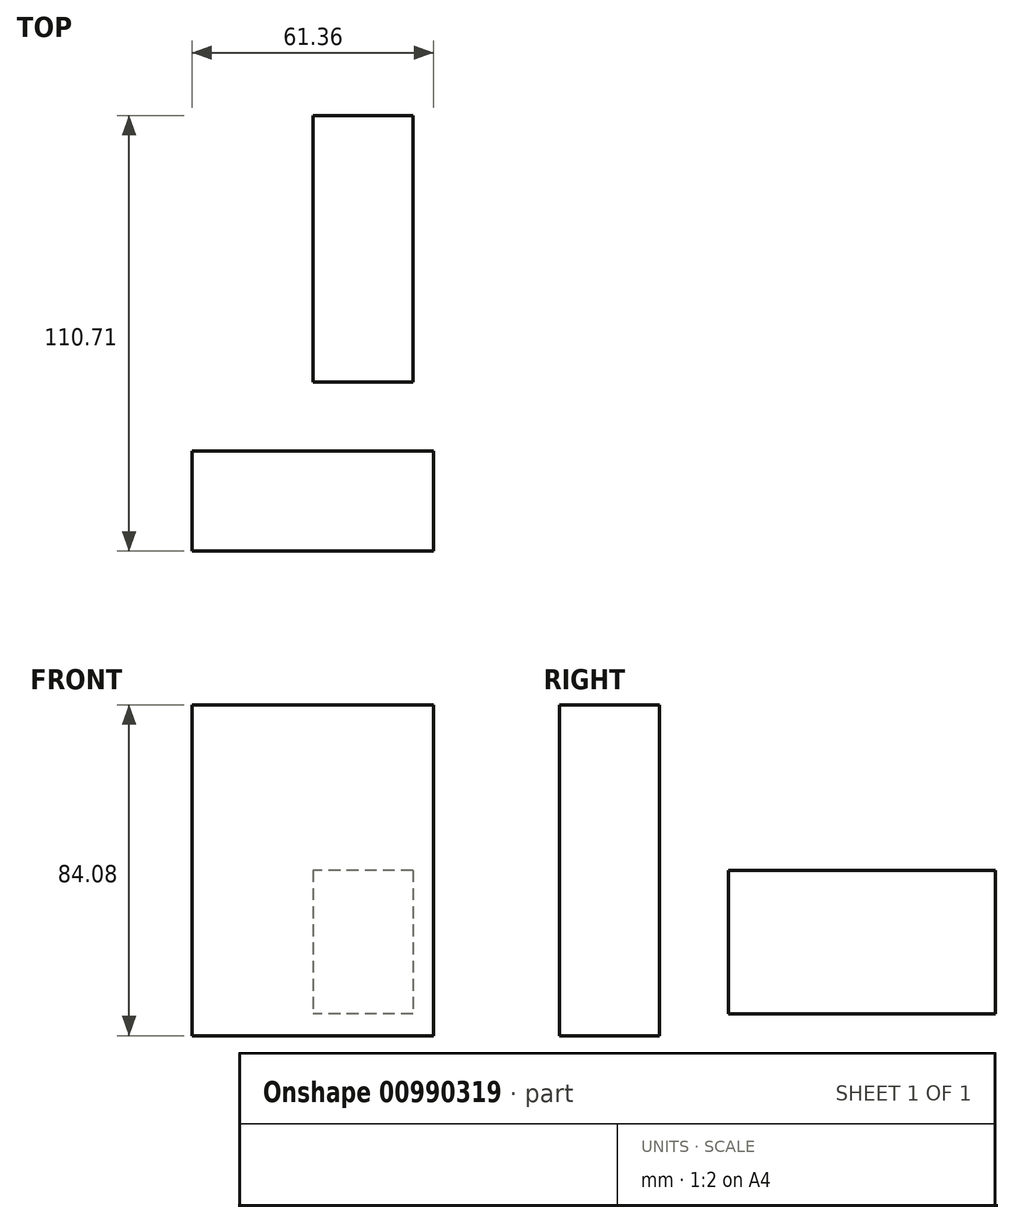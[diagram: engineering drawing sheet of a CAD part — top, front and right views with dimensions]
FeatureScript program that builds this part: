
annotation { "Feature Type Name" : "Feature", "Feature Type Description" : "" }
export const myFeature = defineFeature(function(context is Context, id is Id, definition is map)
    precondition{}
    {
        {
            var Q0;
            Q0=qCreatedBy(makeId("Front.planeOp"),FACE);
            var sketch = newSketch(context, id + "F0", { "sketchPlane" : qUnion([Q0])});
            skLineSegment(sketch, "E0.bottom", {"start": v(30.68, 42.04) * mm, "end": v(-30.68, 42.04) * mm});
            skLineSegment(sketch, "E0.top", {"start": v(30.68, -42.04) * mm, "end": v(-30.68, -42.04) * mm});
            skLineSegment(sketch, "E0.left", {"start": v(30.68, 42.04) * mm, "end": v(30.68, -42.04) * mm});
            skLineSegment(sketch, "E0.right", {"start": v(-30.68, 42.04) * mm, "end": v(-30.68, -42.04) * mm});
            skPoint(sketch, "E0.middle", {"position": v(0, 0) * mm});
            skSolve(sketch);
        }
        {
            var Q0;
            Q0=makeQuery(id+"F0.imprint","IMPRINT",FACE,{"disambiguationData":[TD([[makeQuery(id+"F0.imprint","IMPRINT",EDGE,{"derivedFrom":sQuery(id+"F0.wireOp",EDGE,"E0.bottom")}),1.0]])]});
            extrude(context, id + "F1", {"entities" : qUnion([Q0]), "depth" : 25.4 * mm, "offsetDistance" : 25.4 * mm});
        }
        {
            var Q0;
            Q0=qCreatedBy(makeId("Right.planeOp"),FACE);
            var sketch = newSketch(context, id + "F2", { "sketchPlane" : qUnion([Q0])});
            skLineSegment(sketch, "E1.bottom", {"start": v(85.3, 0) * mm, "end": v(17.54, 0) * mm});
            skLineSegment(sketch, "E1.top", {"start": v(85.3, -36.5) * mm, "end": v(17.54, -36.5) * mm});
            skLineSegment(sketch, "E1.left", {"start": v(85.3, 0) * mm, "end": v(85.3, -36.5) * mm});
            skLineSegment(sketch, "E1.right", {"start": v(17.54, 0) * mm, "end": v(17.54, -36.5) * mm});
            skPoint(sketch, "E1.middle", {"position": v(51.42, -18.25) * mm});
            skSolve(sketch);
        }
        {
            var Q0;
            Q0 = qSketchRegion(id + "F2", true);
            extrude(context, id + "F3", {"entities" : qUnion([Q0]), "depth" : 25.4 * mm, "offsetDistance" : 25.4 * mm});
        }
    });
